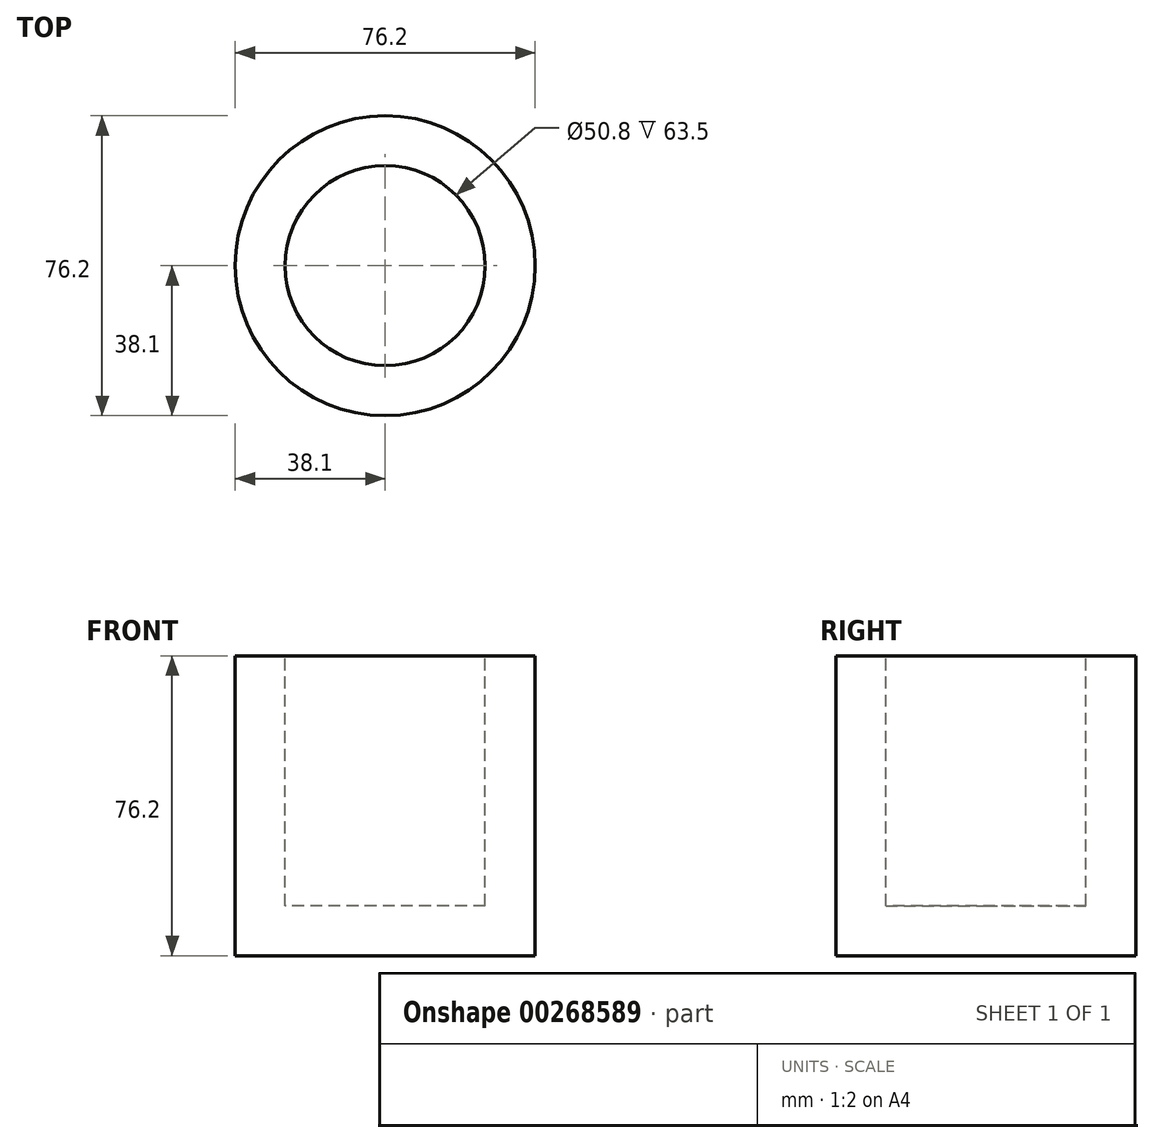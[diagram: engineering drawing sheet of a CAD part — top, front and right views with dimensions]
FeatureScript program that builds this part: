
annotation { "Feature Type Name" : "Feature", "Feature Type Description" : "" }
export const myFeature = defineFeature(function(context is Context, id is Id, definition is map)
    precondition{}
    {
        {
            var Q0;
            Q0=qCreatedBy(makeId("Top.planeOp"),FACE);
            var sketch = newSketch(context, id + "F0", { "sketchPlane" : qUnion([Q0])});
            skCircle(sketch, "E0", {"center": v(0, 0) * mm, "radius": 38.1 * mm});
            skSolve(sketch);
        }
        {
            var Q0;
            Q0 = qSketchRegion(id + "F0", true);
            extrude(context, id + "F1", {"entities" : qUnion([Q0]), "oppositeDirection" : true, "depth" : 38.1 * mm});
        }
        {
            var Q0;
            Q0=makeQuery(id+"F1.opExtrude","CAP_FACE",FACE,{"disambiguationData":[OSD([sQuery(id+"F0.wireOp",EDGE,"E0")])],"isStart":true});
            extrude(context, id + "F2", {"entities" : qUnion([Q0]), "operationType" : NewBodyOperationType.ADD, "depth" : 38.1 * mm});
        }
        {
            var Q0;
            Q0=makeQuery(id+"F2.opExtrude","CAP_FACE",FACE,{"disambiguationData":[OSD([sQuery(id+"F0.wireOp",EDGE,"E0")])],"isStart":false});
            shell(context, id + "F3", {"entities" : qUnion([Q0]), "thickness" : 12.7 * mm});
        }
    });
